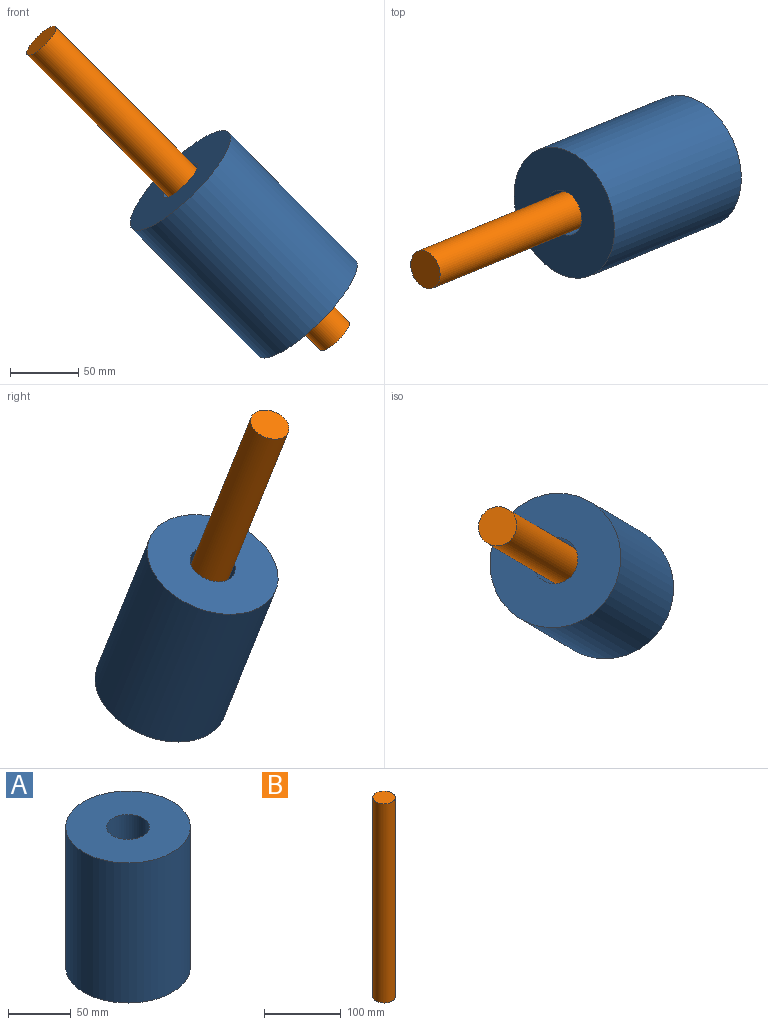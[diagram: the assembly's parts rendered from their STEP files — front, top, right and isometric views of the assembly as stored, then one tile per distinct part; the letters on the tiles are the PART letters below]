
ASSEMBLY  parts=2 mates=1
PART A: 4 faces, bbox 99.8x99.8x137.2 mm
  f0: cylinder r=17.21mm len=137.19mm, axis (0,0,-1), area 14836.5mm2, adj f2,f3
  f1: cylinder r=49.9mm len=137.19mm, axis (0,0,-1), area 43012.7mm2, adj f2,f3
  f2: plane 99.8x99.8mm, normal (0,0,1), area 6891.4mm2, adj f0,f1
  f3: plane 99.8x99.8mm, normal (0,0,-1), area 6891.4mm2, adj f0,f1
PART B: 3 faces, bbox 29.2x29.2x317.4 mm
  f0: cylinder r=14.62mm len=317.43mm, axis (0,0,-1), area 29160mm2, adj f1,f2
  f1: plane 29.24x29.24mm, normal (0,0,1), area 671.5mm2, adj f0
  f2: plane 29.24x29.24mm, normal (0,0,-1), area 671.5mm2, adj f0
PLACE A rot(axis=(-0.93,0.07,-0.36),159.3deg) t=(-41.95,-67.14,-115.05)mm
PLACE B rot(axis=(0.44,-0.88,-0.17),47.8deg) t=(18.89,-42.11,-176.29)mm
MATE slider A.f1 <-> B.f0  axis (-0.68,-0.28,0.68) through (-41.95,-67.14,-115.05)mm
